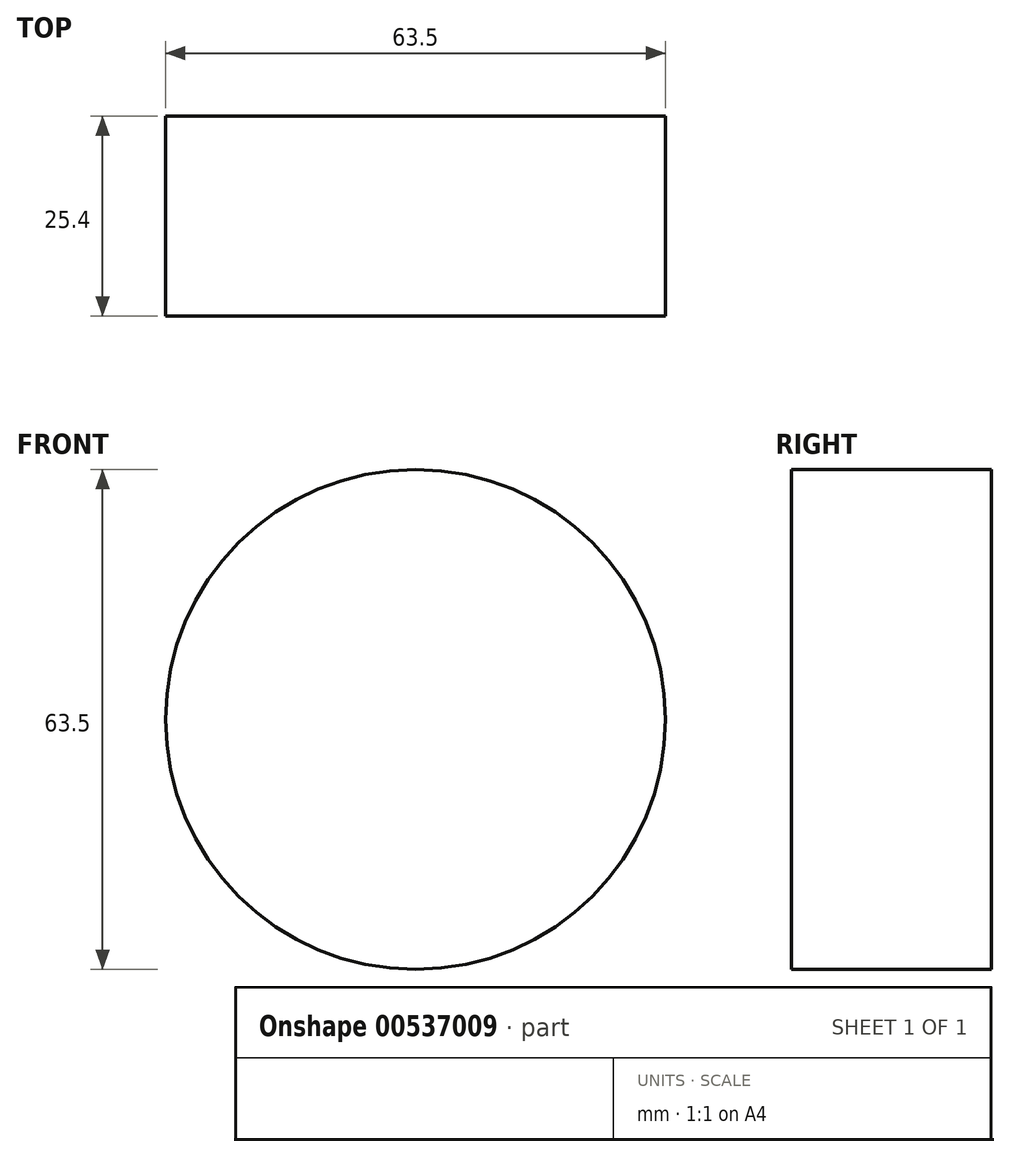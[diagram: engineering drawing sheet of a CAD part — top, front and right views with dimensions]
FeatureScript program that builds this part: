
annotation { "Feature Type Name" : "Feature", "Feature Type Description" : "" }
export const myFeature = defineFeature(function(context is Context, id is Id, definition is map)
    precondition{}
    {
        {
            var Q0;
            Q0=qCreatedBy(makeId("Front.planeOp"),FACE);
            var sketch = newSketch(context, id + "F0", { "sketchPlane" : qUnion([Q0])});
            skCircle(sketch, "E0", {"center": v(0, 0) * mm, "radius": 31.75 * mm});
            skSolve(sketch);
        }
        {
            var Q0;
            Q0=makeQuery(id+"F0.imprint","IMPRINT",FACE,{"disambiguationData":[TD([[makeQuery(id+"F0.imprint","IMPRINT",EDGE,{"derivedFrom":sQuery(id+"F0.wireOp",EDGE,"E0")}),1.0]])]});
            extrude(context, id + "F1", {"entities" : qUnion([Q0]), "depth" : 25.4 * mm, "offsetDistance" : 25.4 * mm});
        }
    });
